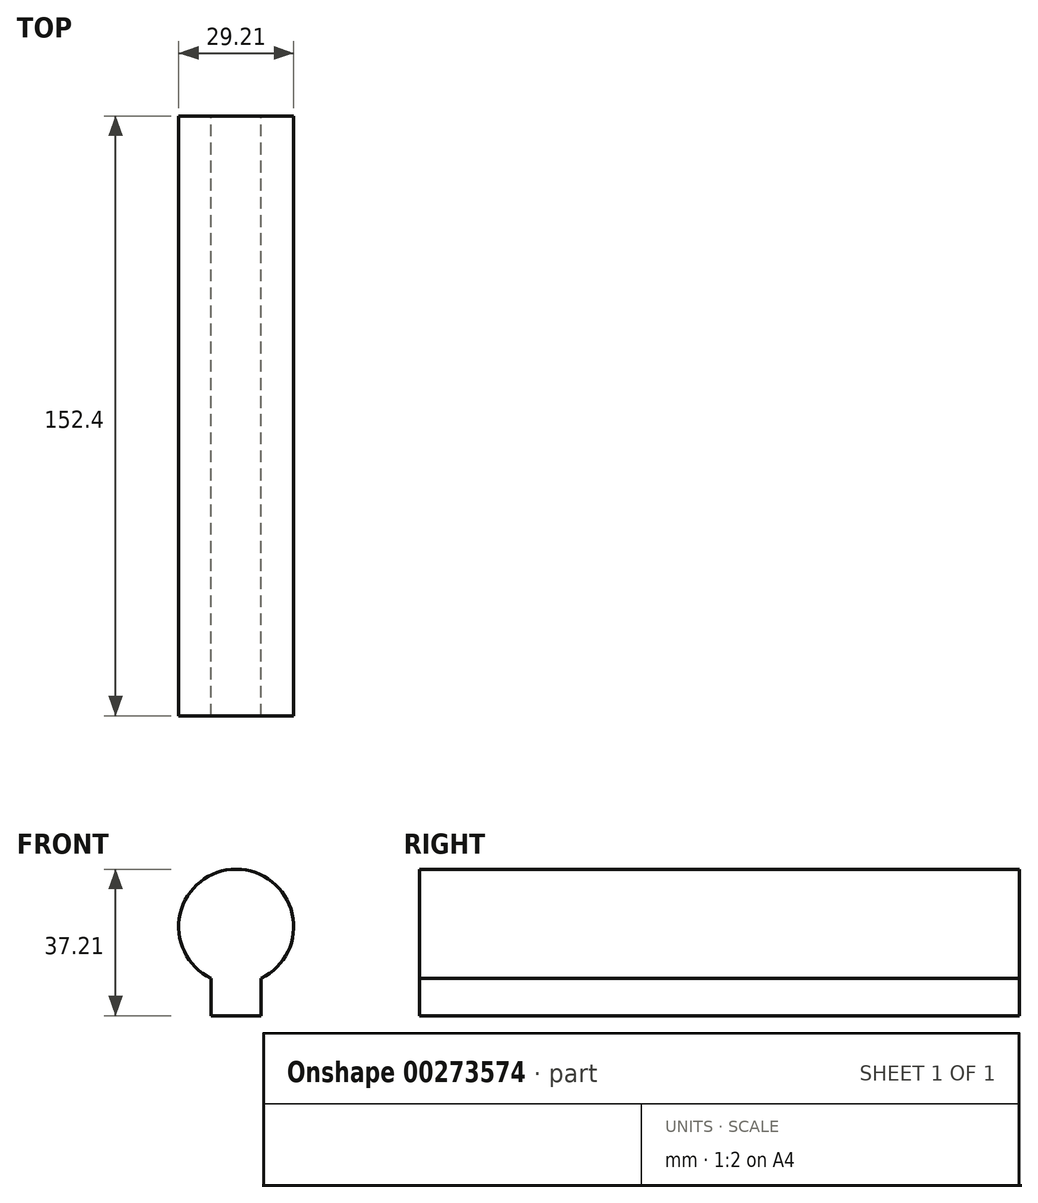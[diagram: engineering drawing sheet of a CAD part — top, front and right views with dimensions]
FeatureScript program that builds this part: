
annotation { "Feature Type Name" : "Feature", "Feature Type Description" : "" }
export const myFeature = defineFeature(function(context is Context, id is Id, definition is map)
    precondition{}
    {
        {
            var Q0;
            Q0=qCreatedBy(makeId("Front.planeOp"),FACE);
            var sketch = newSketch(context, id + "F0", { "sketchPlane" : qUnion([Q0])});
            skArc(sketch, "E0", {"start": v(6.35, -13.15) * mm, "mid": v(0, 14.6) * mm, "end": v(-6.35, -13.15) * mm});
            skLineSegment(sketch, "E1.top", {"start": v(-6.35, -22.6) * mm, "end": v(6.35, -22.6) * mm});
            skLineSegment(sketch, "E1.left", {"start": v(-6.35, -13.15) * mm, "end": v(-6.35, -22.6) * mm});
            skLineSegment(sketch, "E1.right", {"start": v(6.35, -13.15) * mm, "end": v(6.35, -22.6) * mm});
            skPoint(sketch, "E1.middle", {"position": v(0, -14.6) * mm});
            skPoint(sketch, "E2.orphan", {"position": v(-6.35, -6.6) * mm});
            skPoint(sketch, "E3.orphan", {"position": v(6.35, -6.6) * mm});
            skSolve(sketch);
        }
        {
            var Q0;
            Q0=makeQuery(id+"F0.imprint","IMPRINT",FACE,{"disambiguationData":[TD([[makeQuery(id+"F0.imprint","IMPRINT",EDGE,{"derivedFrom":sQuery(id+"F0.wireOp",EDGE,"E0")}),1.0]])]});
            extrude(context, id + "F1", {"entities" : qUnion([Q0]), "depth" : 152.4 * mm});
        }
    });
